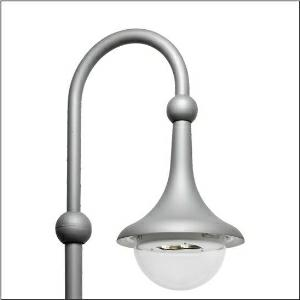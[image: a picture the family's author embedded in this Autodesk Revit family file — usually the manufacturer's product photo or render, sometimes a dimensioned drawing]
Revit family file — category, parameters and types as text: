
# Revit family: grosse_glocke_iq___st1_2a_5xa1565e1v108_00bb
name_source: partatom
category: Lighting Fixtures
units: mm (PartAtom-declared; Revit-internal decimal feet)

## family parameters
Cut with Voids When Loaded = No
Host = Face
Light Source = No
Part Type = Normal
Room Calculation Point = No
Round Connector Dimension = Use Diameter
Shared = No

## types (1)
- --- (1 x LED, 5180 lm, 34.3 W, 3000K)
    Apparent Load = 34 VA
    CIE Flux Codes = 28 66 95 100 100
    Color Rendering = 70
    Color Temperature = 3000K
    Default Elevation = 1800 mm
    Description = Large Bell iQ, mast luminaire, primary light control with 3 zone facetted reflector, of plastic, silver coated, primary optical cover: enclosure, of PMMA, transparent, light distribution: ST1.2a, light emission: direct distribution, primary light characteristic: asymmetric, installation type: suspended mounting, High Power LED, rated luminous flux: 5.180lm, luminous efficacy: 151lm/W, light colour: 730, colour temperature: 3000K, control gear: iQ-Street Remote, D4i with power reduction, control: optimised constant luminous flux control (CLO 2.0), Desk-Remote (wireless, voltage-free reading and setting of iQ features in the workshop via application-optimized NFC function/RFID function), Light-Fading, Smart-Wire, Night-Set, Lumen-Switch, Temp-Guard, Auto-Match, Street-Remote, pre-setting: logarithmic dimming characteristic, mains connection: 230..240V, AC, 50/60Hz, start of lifetime: 34W, end of service life: 38W, reduction: 16W, luminaire housing, bell-shaped, of glass-fibre reinforced polyester, coated, Siteco® metallic grey (DB 702S), please order curved mast extension separately, diameter: 530mm, height: 695mm, mounting height: 4..6m, Smart Interface above, protection rating (complete): IP54, insulation class (complete): insulation class II (safety insulation), certification: CE, ENEC, VDE, impact resistance: IK08, standard-compliant lighting for roads and squares, packaging unit: 1 piece

Light Distribution: ST1.2a
    Height = 695 mm
    Lamp = 1 x LED
    Lamp Light Flux = 5180 lm
    Lamp Power = 34.3 W
    Lamp count = 1
    Length = 530 mm
    Luminous efficacy = 151 lm/W
    Manufacturer = Siteco
    ModVariant = No
    Model = 5XA1565E1V108
    Number of Poles = 1
    OnlyDefault = Yes
    Power Factor = 1
    Product Name = Große Glocke iQ | ST1.2a
    Product group = mast luminaire | pylon annexe
    ProductGroupID = 6200
    Protection Class = Protection class II
    Protection Degree = IP 54
    RLX_Detail_Level = 1
    RLX_Emergency_Light_Flux = 0 lm
    RLX_Emergency_Type = 0
    RLX_Emergency_Type_DB = No
    RlxData = <blob elided: 85317 chars, md5=16bd9535>
    Socket = socket
    Standby Power = 0 W
    System Light Flux = 5180 lm
    System Power = 34 W
    Type Comments = factory setting: luminous flux: 100 % | dim-lin: 254 | 640 mA
    Type Image = l_1347688.jpg
    URL = http://relux.com
    VarID = @adj_066161
    Voltage = 0 V
    Weight = 0.00 kg
    Width = 0 mm  [stored 0 ft]

note: [stored X ft] marks values corroborated as IEEE doubles in the binary element streams (Revit-internal decimal feet)

## geometry (parser evidence)
native form markers: Blend x4, Sweep x11
no freeform markers — native parametric forms only
